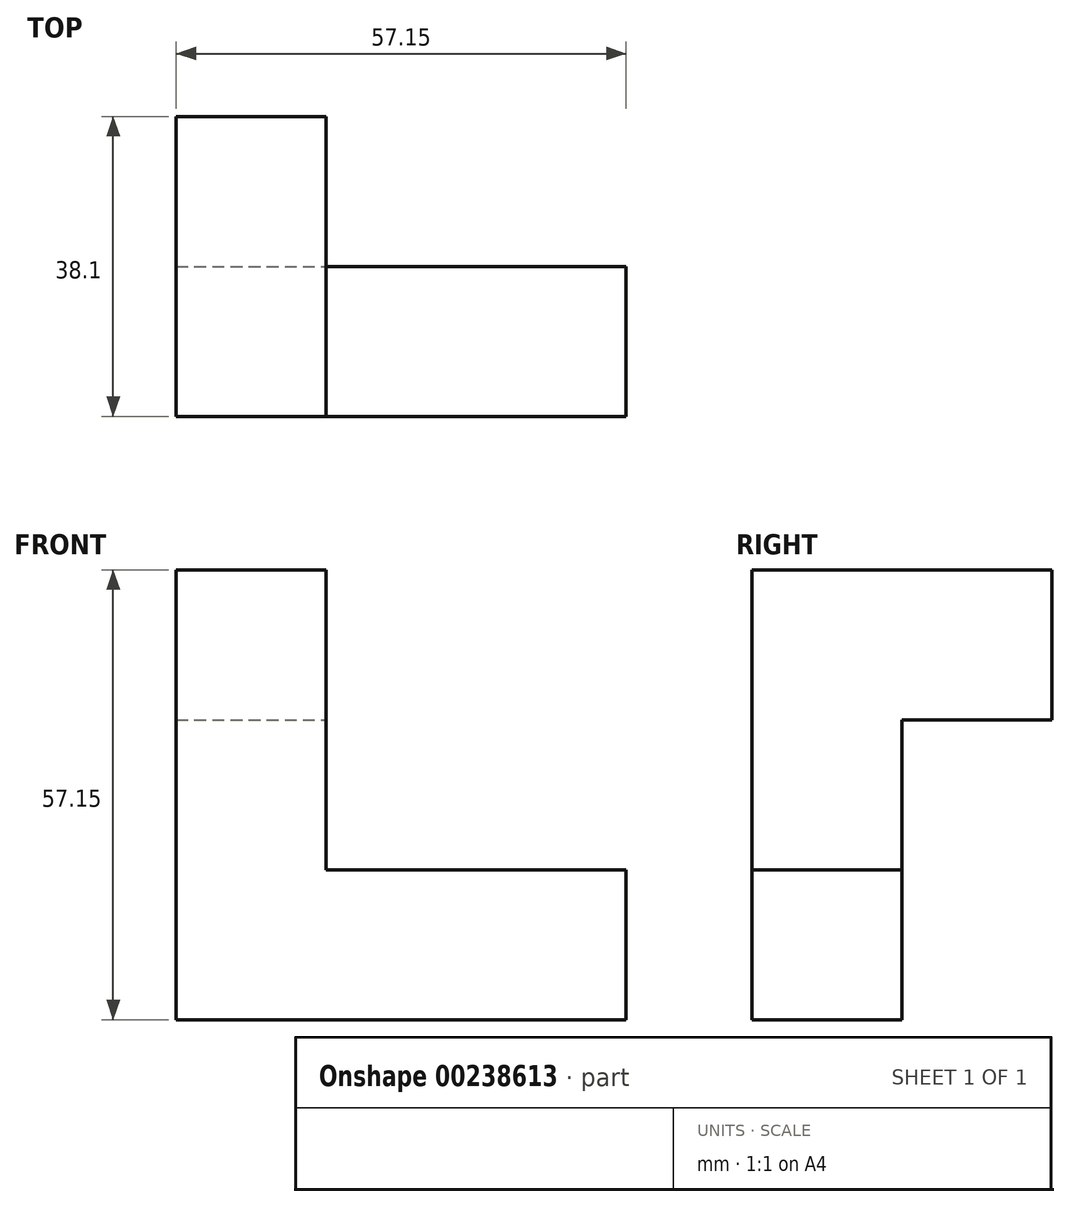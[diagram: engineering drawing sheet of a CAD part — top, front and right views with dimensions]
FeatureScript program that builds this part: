
annotation { "Feature Type Name" : "Feature", "Feature Type Description" : "" }
export const myFeature = defineFeature(function(context is Context, id is Id, definition is map)
    precondition{}
    {
        {
            var Q0;
            Q0=qCreatedBy(makeId("Front.planeOp"),FACE);
            var sketch = newSketch(context, id + "F0", { "sketchPlane" : qUnion([Q0])});
            skLineSegment(sketch, "E0", {"start": v(0, 0) * mm, "end": v(38.1, 0) * mm});
            skLineSegment(sketch, "E1", {"start": v(38.1, 0) * mm, "end": v(38.1, -19.05) * mm});
            skLineSegment(sketch, "E2", {"start": v(38.1, -19.05) * mm, "end": v(-19.05, -19.05) * mm});
            skLineSegment(sketch, "E3", {"start": v(-19.05, -19.05) * mm, "end": v(-19.05, 38.1) * mm});
            skLineSegment(sketch, "E4", {"start": v(-19.05, 38.1) * mm, "end": v(0, 38.1) * mm});
            skLineSegment(sketch, "E5", {"start": v(0, 38.1) * mm, "end": v(0, 0) * mm});
            skSolve(sketch);
        }
        {
            var Q0;
            Q0 = qSketchRegion(id + "F0", true);
            extrude(context, id + "F1", {"entities" : qUnion([Q0]), "depth" : 19.05 * mm});
        }
        {
            var Q0;
            Q0=makeQuery(id+"F1.opExtrude","CAP_FACE",FACE,{"disambiguationData":[OSD([sQuery(id+"F0.wireOp",EDGE,"E0"),sQuery(id+"F0.wireOp",EDGE,"E1"),sQuery(id+"F0.wireOp",EDGE,"E2"),sQuery(id+"F0.wireOp",EDGE,"E3"),sQuery(id+"F0.wireOp",EDGE,"E4"),sQuery(id+"F0.wireOp",EDGE,"E5")])],"isStart":true});
            var sketch = newSketch(context, id + "F2", { "sketchPlane" : qUnion([Q0])});
            skLineSegment(sketch, "E6.bottom", {"start": v(19.05, 38.1) * mm, "end": v(0, 38.1) * mm});
            skLineSegment(sketch, "E6.top", {"start": v(19.05, 19.05) * mm, "end": v(0, 19.05) * mm});
            skLineSegment(sketch, "E6.left", {"start": v(19.05, 38.1) * mm, "end": v(19.05, 19.05) * mm});
            skLineSegment(sketch, "E6.right", {"start": v(0, 38.1) * mm, "end": v(0, 19.05) * mm});
            skSolve(sketch);
        }
        {
            var Q0;
            Q0 = qSketchRegion(id + "F2", true);
            extrude(context, id + "F3", {"entities" : qUnion([Q0]), "operationType" : NewBodyOperationType.ADD, "depth" : 19.05 * mm});
        }
    });
